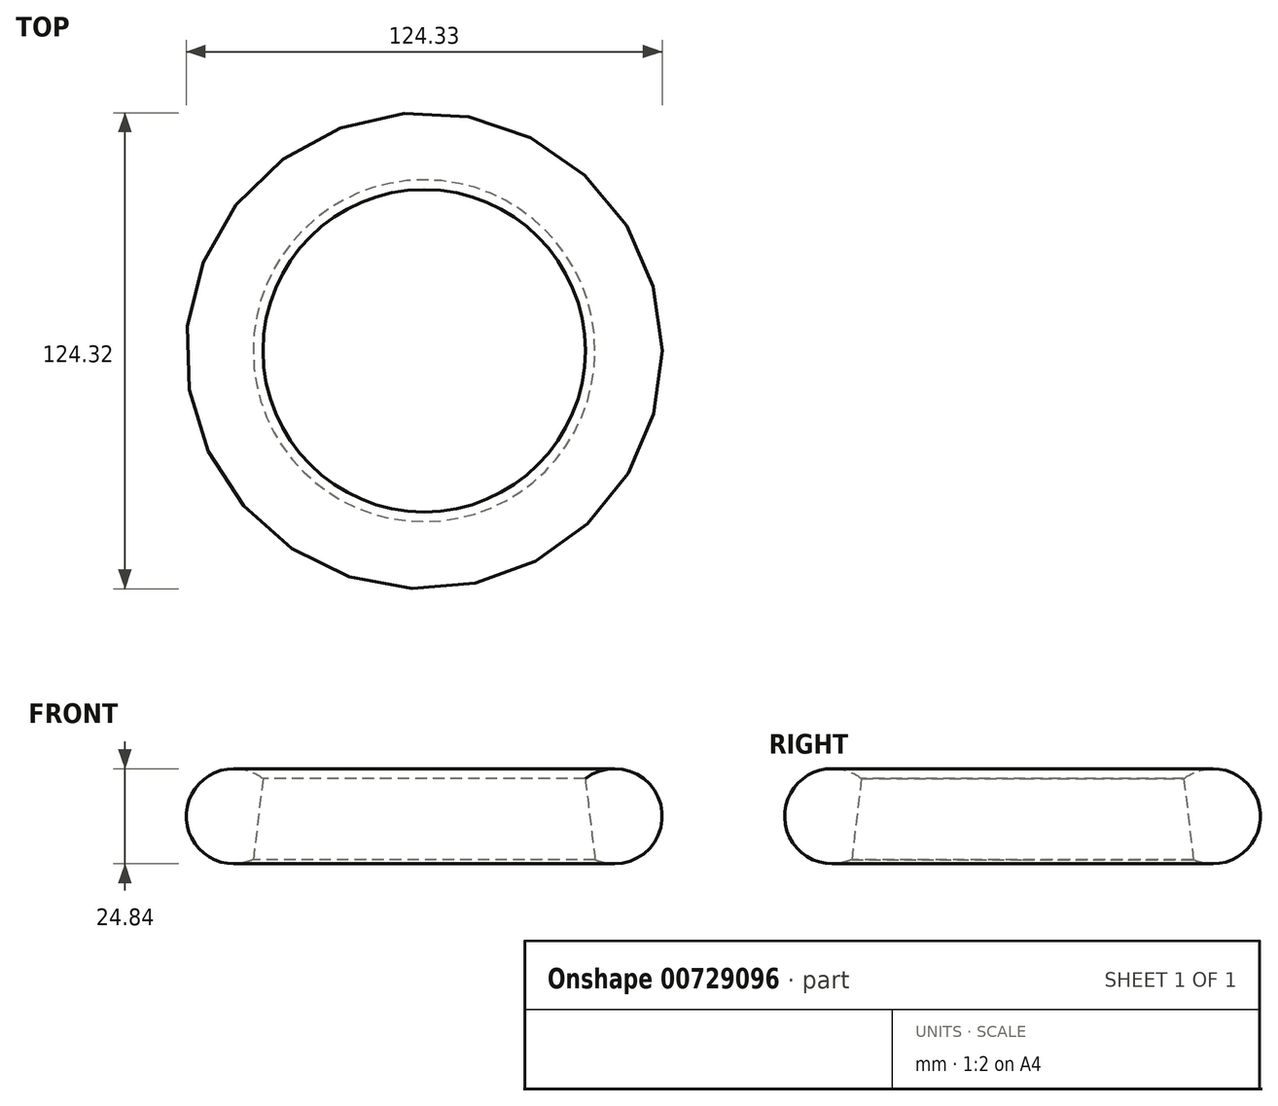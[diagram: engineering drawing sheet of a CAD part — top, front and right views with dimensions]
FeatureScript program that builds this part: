
annotation { "Feature Type Name" : "Feature", "Feature Type Description" : "" }
export const myFeature = defineFeature(function(context is Context, id is Id, definition is map)
    precondition{}
    {
        {
            var Q0;
            Q0=qCreatedBy(makeId("Top.planeOp"),FACE);
            var sketch = newSketch(context, id + "F0", { "sketchPlane" : qUnion([Q0])});
            skCircle(sketch, "E0.cCircle", {"center": v(0, 0) * mm, "radius": 40.07 * mm, "construction": true});
            skLineSegment(sketch, "E0.0", {"start": v(-38.03, 26.35) * mm, "end": v(3.8, 46.1) * mm});
            skLineSegment(sketch, "E0.1", {"start": v(3.8, 46.1) * mm, "end": v(41.83, 19.76) * mm});
            skLineSegment(sketch, "E0.2", {"start": v(41.83, 19.76) * mm, "end": v(38.03, -26.35) * mm});
            skLineSegment(sketch, "E0.3", {"start": v(38.03, -26.35) * mm, "end": v(-3.8, -46.1) * mm});
            skLineSegment(sketch, "E0.4", {"start": v(-3.8, -46.1) * mm, "end": v(-41.83, -19.76) * mm});
            skLineSegment(sketch, "E0.5", {"start": v(-41.83, -19.76) * mm, "end": v(-38.03, 26.35) * mm});
            skPoint(sketch, "E0.0.midPoint", {"position": v(-17.12, 36.23) * mm});
            skCircle(sketch, "E1", {"center": v(-113.8, 0) * mm, "radius": 49.85 * mm});
            skSolve(sketch);
        }
        {
            var Q0;
            Q0=qCreatedBy(makeId("Front.planeOp"),FACE);
            var sketch = newSketch(context, id + "F1", { "sketchPlane" : qUnion([Q0])});
            skArc(sketch, "E2", {"start": v(-69.16, 0) * mm, "mid": v(-51.72, 12.8) * mm, "end": v(-71.7, 21.1) * mm});
            skLineSegment(sketch, "E3", {"start": v(-71.7, 21.1) * mm, "end": v(-69.16, 0) * mm});
            skSolve(sketch);
        }
        {
            var Q0;
            Q0=makeQuery(id+"F1.imprint","IMPRINT",FACE,{"disambiguationData":[TD([[makeQuery(id+"F1.imprint","IMPRINT",EDGE,{"derivedFrom":sQuery(id+"F1.wireOp",EDGE,"E2")}),1.0]])]});
            var Q1;
            Q1=sQuery(id+"F0.wireOp",EDGE,"E1");
            sweep(context, id + "F2", {"profiles" : qUnion([Q0]), "path" : qUnion([Q1])});
        }
    });
